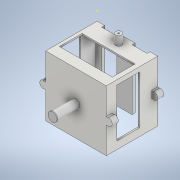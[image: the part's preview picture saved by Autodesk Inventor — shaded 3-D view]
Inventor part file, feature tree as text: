
AUTODESK INVENTOR PART (.ipt)
format: ipt  version: 2021 (Build 250183000, 183)  size: 302,592 bytes
history: native  units: mm
features: sketch x19, extrude x15, other x1, hole x1
ambient origin geometry x8: Origin, YZ Plane, XZ Plane, XY Plane, X Axis, Y Axis, Z Axis, Center Point
bodies: Body1 (feature_tree), Body2 (feature_tree), Body3 (feature_tree), Body4 (feature_tree)
feature tree (36):
  other  "Sólido1"
  extrude  "Extrusão1"  Depth=40.0mm
  extrude  "Extrusão2"  Depth=10.0mm TaperAngle=0.0deg
  extrude  "Extrusão3"  Depth=20.0mm TaperAngle=0.0deg
  extrude  "Extrusão4"  Depth=5.0mm TaperAngle=0.0deg
  sketch  "Esboço5"  dims[d14=5.0mm d15=0.0mm d16=5.0mm d17=0.0mm]
  extrude  "Extrusão5"  Depth=5.0mm TaperAngle=0.0deg
  extrude  "Extrusão6"  Depth=4.0mm
  extrude  "Extrusão7"  Depth=5.0mm
  extrude  "Extrusão8"  Depth=4.0mm TaperAngle=0.0deg
  extrude  "Extrusão9"  Depth=15.0mm TaperAngle=0.0deg
  extrude  "Extrusão10"  Depth=0.5mm TaperAngle=0.0deg
  sketch  "Esboço12"  dims[d44=10.0mm d45=10.0mm]
  hole  "Furo1"  [1 undecoded]
  extrude  "Extrusão11"  Depth=10.0mm TaperAngle=0.0deg
  extrude  "Extrusão12"  [1 undecoded]
  sketch  "Esboço16"
  extrude  "Extrusão13"  [1 undecoded]
  extrude  "Extrusão14"  [1 undecoded]
  extrude  "Extrusão15"  [1 undecoded]
  sketch  "Esboço1"  dims[d0=40.0mm d1=40.0mm]
  sketch  "Esboço2"  dims[d2=2.0mm d3=0.0mm d4=10.0mm d5=0.0mm]
  sketch  "Esboço3"  dims[d6=20.0mm d7=0.0mm d8=20.0mm d9=0.0mm]
  sketch  "Esboço4"  dims[d10=20.0mm d11=0.0mm d12=5.0mm d13=0.0mm]
  sketch  "Esboço6"  dims[d18=2.0mm d19=0.0mm d20=4.0mm]
  sketch  "Esboço7"  dims[d21=6.0mm d22=0.0mm]
  sketch  "Esboço8"  dims[d23=1.01092mm d24=2.388mm d25=4.0mm d26=2.0mm d27=90.0deg d28=3.799mm d29=0.0mm d30=5.0mm]
  sketch  "Esboço9"  dims[d31=4.0mm d32=0.0mm d34=4.0mm d35=0.0mm]
  sketch  "Esboço10"  dims[d36=5.0mm d37=15.0mm d38=0.0mm]
  sketch  "Esboço11"  dims[d39=6.0mm d40=0.5mm d41=0.0mm]
  sketch  "Esboço13"  dims[d46=40.0mm d47=10.0mm d48=0.0mm]
  sketch  "Esboço14"  dims[d33=0.5mm]
  sketch  "Esboço15"
  sketch  "Esboço17"
  sketch  "Esboço18"
  sketch  "Esboço20"
note: 5 required parameter values undecoded (feature->parameter linkage not recoverable at this tier; creation-order binding heuristic only, values carry confidence <= 0.55)
